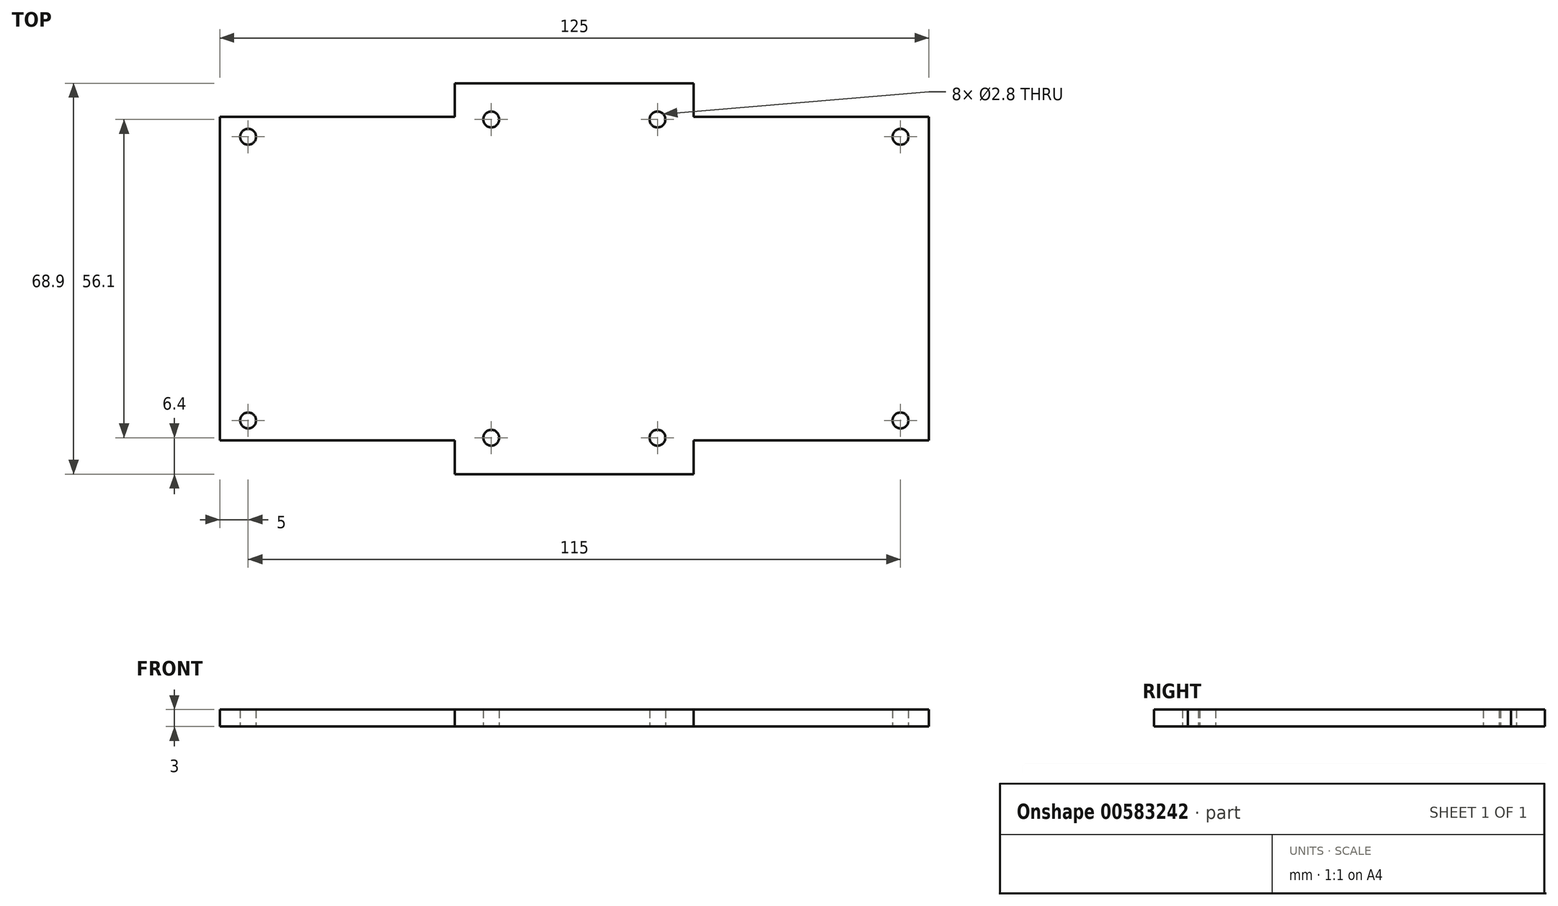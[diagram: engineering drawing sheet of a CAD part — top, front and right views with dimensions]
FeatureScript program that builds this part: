
annotation { "Feature Type Name" : "Feature", "Feature Type Description" : "" }
export const myFeature = defineFeature(function(context is Context, id is Id, definition is map)
    precondition{}
    {
        {
            var Q0;
            Q0=qCreatedBy(makeId("Top.planeOp"),FACE);
            var sketch = newSketch(context, id + "F0", { "sketchPlane" : qUnion([Q0])});
            skLineSegment(sketch, "E0.bottom", {"start": v(18.05, -31.45) * mm, "end": v(-18.05, -31.45) * mm, "construction": true});
            skLineSegment(sketch, "E0.top", {"start": v(18.05, 31.45) * mm, "end": v(-18.05, 31.45) * mm, "construction": true});
            skLineSegment(sketch, "E0.left", {"start": v(18.05, -31.45) * mm, "end": v(18.05, 31.45) * mm, "construction": true});
            skLineSegment(sketch, "E0.right", {"start": v(-18.05, -31.45) * mm, "end": v(-18.05, 31.45) * mm, "construction": true});
            skPoint(sketch, "E0.middle", {"position": v(0, 0) * mm});
            skCircle(sketch, "E1", {"center": v(-14.65, -28.05) * mm, "radius": 1.65 * mm, "construction": true});
            skCircle(sketch, "E2", {"center": v(-14.65, 28.05) * mm, "radius": 1.65 * mm, "construction": true});
            skCircle(sketch, "E3", {"center": v(14.65, 28.05) * mm, "radius": 1.65 * mm, "construction": true});
            skCircle(sketch, "E4", {"center": v(14.65, -28.05) * mm, "radius": 1.65 * mm, "construction": true});
            skCircle(sketch, "E5", {"center": v(14.65, -28.05) * mm, "radius": 1.4 * mm});
            skCircle(sketch, "E6", {"center": v(-14.65, -28.05) * mm, "radius": 1.4 * mm});
            skCircle(sketch, "E7", {"center": v(-14.65, 28.05) * mm, "radius": 1.4 * mm});
            skCircle(sketch, "E8", {"center": v(14.65, 28.05) * mm, "radius": 1.4 * mm});
            skLineSegment(sketch, "E9.bottom", {"start": v(62.5, -40) * mm, "end": v(-62.5, -40) * mm, "construction": true});
            skLineSegment(sketch, "E9.top", {"start": v(62.5, 40) * mm, "end": v(-62.5, 40) * mm, "construction": true});
            skLineSegment(sketch, "E9.left", {"start": v(62.5, -40) * mm, "end": v(62.5, 40) * mm, "construction": true});
            skLineSegment(sketch, "E9.right", {"start": v(-62.5, -40) * mm, "end": v(-62.5, 40) * mm, "construction": true});
            skCircle(sketch, "E10", {"center": v(-57.5, 25) * mm, "radius": 1.4 * mm});
            skCircle(sketch, "E11", {"center": v(-57.5, -25) * mm, "radius": 1.4 * mm});
            skCircle(sketch, "E12", {"center": v(57.5, -25) * mm, "radius": 1.4 * mm});
            skCircle(sketch, "E13", {"center": v(57.5, 25) * mm, "radius": 1.4 * mm});
            skLineSegment(sketch, "E14", {"start": v(-62.5, 28.5) * mm, "end": v(-62.5, -28.5) * mm});
            skLineSegment(sketch, "E15", {"start": v(-62.5, -28.5) * mm, "end": v(-21.05, -28.5) * mm});
            skLineSegment(sketch, "E16", {"start": v(-21.05, -28.5) * mm, "end": v(-21.05, -34.45) * mm});
            skLineSegment(sketch, "E17", {"start": v(-21.05, -34.45) * mm, "end": v(21.05, -34.45) * mm});
            skLineSegment(sketch, "E18", {"start": v(21.05, -34.45) * mm, "end": v(21.05, -28.5) * mm});
            skLineSegment(sketch, "E19", {"start": v(21.05, -28.5) * mm, "end": v(62.5, -28.5) * mm});
            skLineSegment(sketch, "E20", {"start": v(62.5, -28.5) * mm, "end": v(62.5, 28.5) * mm});
            skLineSegment(sketch, "E21", {"start": v(62.5, 28.5) * mm, "end": v(21.05, 28.5) * mm});
            skLineSegment(sketch, "E22", {"start": v(21.05, 28.5) * mm, "end": v(21.05, 34.45) * mm});
            skLineSegment(sketch, "E23", {"start": v(21.05, 34.45) * mm, "end": v(-21.05, 34.45) * mm});
            skLineSegment(sketch, "E24", {"start": v(-21.05, 34.45) * mm, "end": v(-21.05, 28.5) * mm});
            skLineSegment(sketch, "E25", {"start": v(-21.05, 28.5) * mm, "end": v(-62.5, 28.5) * mm});
            skSolve(sketch);
        }
        {
            var Q0;
            Q0=makeQuery(id+"F0.imprint","IMPRINT",FACE,{"disambiguationData":[TD([[makeQuery(id+"F0.imprint","IMPRINT",EDGE,{"derivedFrom":sQuery(id+"F0.wireOp",EDGE,"E5")}),-1.0]])]});
            extrude(context, id + "F1", {"entities" : qUnion([Q0]), "depth" : 3 * mm, "offsetDistance" : 25 * mm});
        }
    });
